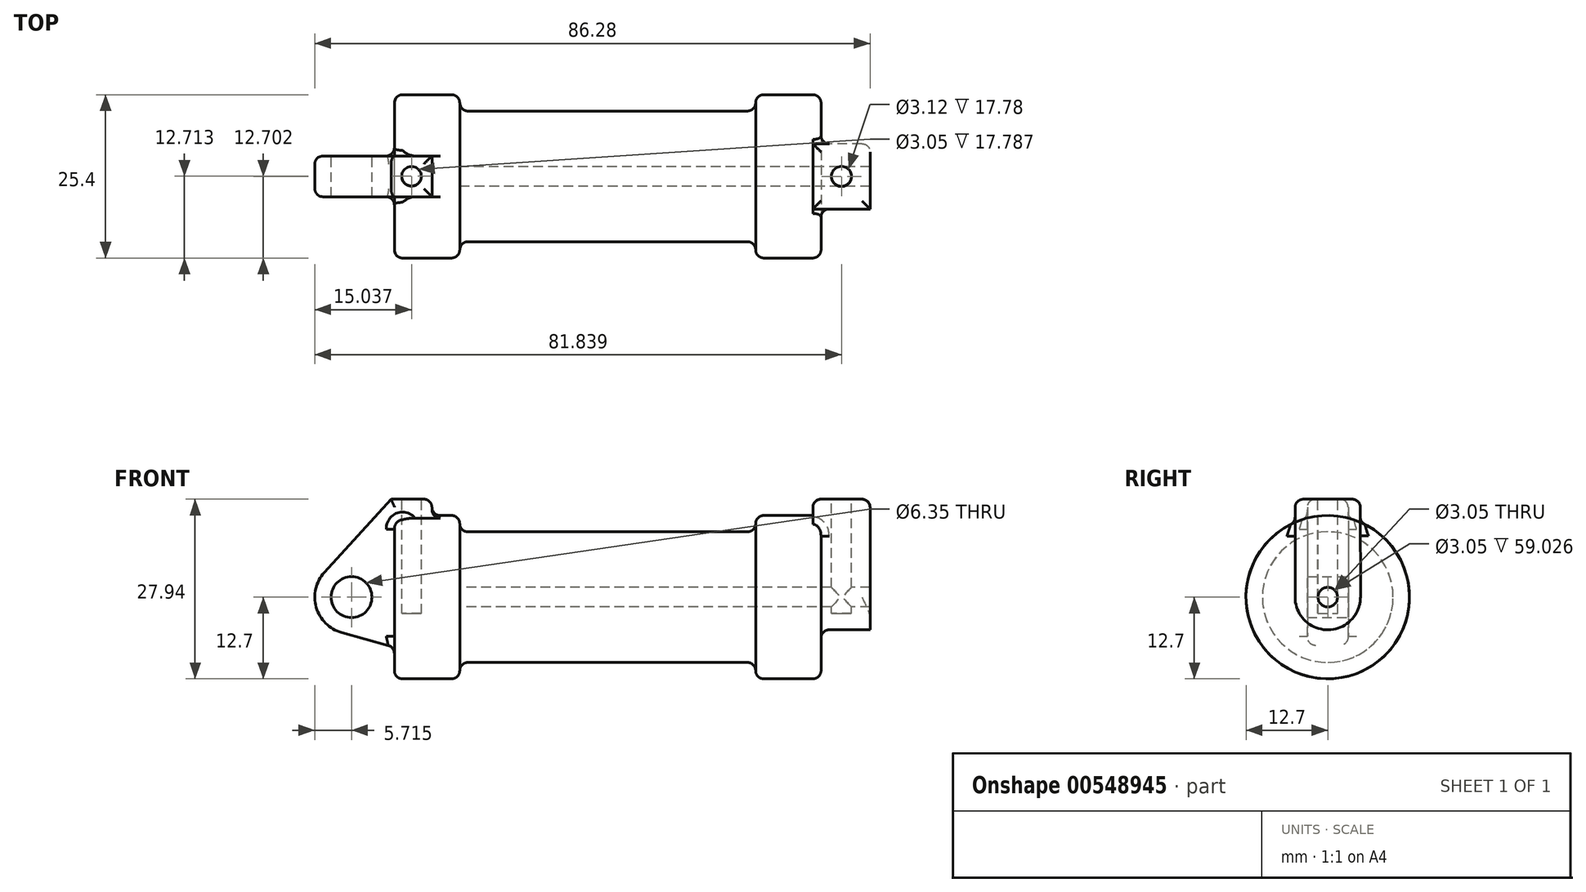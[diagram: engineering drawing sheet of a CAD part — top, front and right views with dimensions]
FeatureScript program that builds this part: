
annotation { "Feature Type Name" : "Feature", "Feature Type Description" : "" }
export const myFeature = defineFeature(function(context is Context, id is Id, definition is map)
    precondition{}
    {
        {
            var Q0;
            Q0=qCreatedBy(makeId("Front.planeOp"),FACE);
            var sketch = newSketch(context, id + "F0", { "sketchPlane" : qUnion([Q0])});
            skLineSegment(sketch, "E0", {"start": v(0, 0) * mm, "end": v(0, 12.7) * mm});
            skLineSegment(sketch, "E1", {"start": v(0, 12.7) * mm, "end": v(10.16, 12.7) * mm});
            skLineSegment(sketch, "E2", {"start": v(10.16, 12.7) * mm, "end": v(10.16, 10.16) * mm});
            skLineSegment(sketch, "E3", {"start": v(10.16, 10.16) * mm, "end": v(56.13, 10.16) * mm});
            skLineSegment(sketch, "E4", {"start": v(56.13, 10.16) * mm, "end": v(56.13, 12.7) * mm});
            skLineSegment(sketch, "E5", {"start": v(56.13, 12.7) * mm, "end": v(66.3, 12.7) * mm});
            skLineSegment(sketch, "E6", {"start": v(66.3, 12.7) * mm, "end": v(66.3, 0) * mm});
            skLineSegment(sketch, "E7", {"start": v(66.3, 0) * mm, "end": v(0, 0) * mm});
            skLineSegment(sketch, "E8", {"start": v(5.84, 15.24) * mm, "end": v(-0.5, 15.24) * mm});
            skLineSegment(sketch, "E9", {"start": v(-0.5, 15.24) * mm, "end": v(-10.88, 3.85) * mm});
            skLineSegment(sketch, "E10", {"start": v(0, 0) * mm, "end": v(-6.65, 0) * mm});
            skCircle(sketch, "E11", {"center": v(-6.65, 0) * mm, "radius": 5.72 * mm});
            skCircle(sketch, "E12", {"center": v(-6.65, 0) * mm, "radius": 3.18 * mm});
            skLineSegment(sketch, "E13", {"start": v(5.84, 15.24) * mm, "end": v(5.84, -9.4) * mm});
            skLineSegment(sketch, "E14", {"start": v(5.84, -9.4) * mm, "end": v(-8.18, -5.5) * mm});
            skSolve(sketch);
        }
        {
            var Q0;
            {var subQ0=sQuery(id+"F0.wireOp",EDGE,"E2");Q0=makeQuery(id+"F0.imprint","IMPRINT",FACE,{"disambiguationData":[TD([[makeQuery(id+"F0.imprint","IMPRINT",EDGE,{"derivedFrom":subQ0}),-1.0]])]});}
            var Q1;
            {var subQ0=sQuery(id+"F0.wireOp",EDGE,"E0");Q1=makeQuery(id+"F0.imprint","IMPRINT",FACE,{"disambiguationData":[TD([[makeQuery(id+"F0.imprint","IMPRINT",EDGE,{"derivedFrom":subQ0}),-1.0]])]});}
            var Q2;
            Q2=sQuery(id+"F0.wireOp",EDGE,"E10");
            revolve(context, id + "F1", {"entities" : qUnion([Q0, Q1]), "axis" : qUnion([Q2]), "revolveType" : RevolveType.FULL});
        }
        {
            var Q0;
            {var subQ1=sQuery(id+"F0.wireOp",EDGE,"E0");Q0=makeQuery(id+"F0.imprint","IMPRINT",FACE,{"disambiguationData":[TD([[makeQuery(id+"F0.imprint","IMPRINT",EDGE,{"derivedFrom":subQ1}),1.0]])]});}
            var Q1;
            {var subQ0=sQuery(id+"F0.wireOp",EDGE,"E0");Q1=makeQuery(id+"F0.imprint","IMPRINT",FACE,{"disambiguationData":[TD([[makeQuery(id+"F0.imprint","IMPRINT",EDGE,{"derivedFrom":subQ0}),-1.0]])]});}
            var Q2;
            {var subQ5=sQuery(id+"F0.wireOp",EDGE,"E12");Q2=makeQuery(id+"F0.imprint","IMPRINT",FACE,{"disambiguationData":[TD([[makeQuery(id+"F0.imprint","IMPRINT",EDGE,{"derivedFrom":subQ5}),-1.0]])]});}
            var Q3;
            {var subQ0=sQuery(id+"F0.wireOp",EDGE,"E14");Q3=makeQuery(id+"F0.imprint","IMPRINT",FACE,{"disambiguationData":[TD([[makeQuery(id+"F0.imprint","IMPRINT",EDGE,{"derivedFrom":subQ0}),-1.0]])]});}
            extrude(context, id + "F2", {"entities" : qUnion([Q0, Q1, Q2, Q3]), "operationType" : NewBodyOperationType.ADD, "endBound" : BoundingType.SYMMETRIC, "depth" : 6.35 * mm, "offsetDistance" : 25.4 * mm});
        }
        {
            var Q0;
            Q0=makeQuery(id+"F1.opRevolve","SWEPT_FACE",FACE,{"disambiguationData":[OSD([sQuery(id+"F0.wireOp",EDGE,"E6")])]});
            var sketch = newSketch(context, id + "F3", { "sketchPlane" : qUnion([Q0])});
            skCircle(sketch, "E15", {"center": v(0, 0) * mm, "radius": 1.52 * mm});
            skCircle(sketch, "E16", {"center": v(0, 0) * mm, "radius": 5.08 * mm});
            skLineSegment(sketch, "E17.left", {"start": v(-5.08, 0) * mm, "end": v(-5.08, 0) * mm});
            skLineSegment(sketch, "E17.right", {"start": v(5.08, 0) * mm, "end": v(5.08, 0) * mm});
            skLineSegment(sketch, "E18", {"start": v(5.08, 0) * mm, "end": v(5.06, 15.24) * mm});
            skLineSegment(sketch, "E19", {"start": v(5.06, 15.24) * mm, "end": v(-5.08, 15.23) * mm});
            skLineSegment(sketch, "E20", {"start": v(-5.08, 15.23) * mm, "end": v(-5.08, 0) * mm});
            skSolve(sketch);
        }
        {
            var Q0;
            {var subQ0=sQuery(id+"F3.wireOp",EDGE,"E19");Q0=makeQuery(id+"F3.imprint","IMPRINT",FACE,{"disambiguationData":[TD([[makeQuery(id+"F3.imprint","IMPRINT",EDGE,{"derivedFrom":subQ0}),1.0]])]});}
            var Q1;
            {var subQ0=sQuery(id+"F3.wireOp",EDGE,"E18");var subQ1=sQuery(id+"F3.wireOp",EDGE,"E16");var subQ2=makeQuery(id+"F3.imprint","INTERSECT",VERTEX,{"derivedFrom":[subQ1,subQ0]});Q1=makeQuery(id+"F3.imprint","IMPRINT",FACE,{"disambiguationData":[TD([[makeQuery(id+"F3.imprint","IMPRINT",EDGE,{"disambiguationData":[TD([[subQ2,-1.0]])],"derivedFrom":subQ1}),-1.0]])]});}
            var Q2;
            Q2=makeQuery(id+"F3.imprint","IMPRINT",FACE,{"disambiguationData":[TD([[makeQuery(id+"F3.imprint","IMPRINT",EDGE,{"derivedFrom":sQuery(id+"F3.wireOp",EDGE,"E15")}),-1.0]])]});
            extrude(context, id + "F4", {"entities" : qUnion([Q0, Q1, Q2]), "operationType" : NewBodyOperationType.ADD, "depth" : 7.62 * mm, "offsetDistance" : 25.4 * mm, "hasSecondDirection" : true, "secondDirectionOppositeDirection" : true, "secondDirectionDepth" : 1.27 * mm});
        }
        {
            var Q0;
            Q0=makeQuery(id+"F4.boolean.opBoolean","SPLIT",FACE,{"disambiguationData":[TD([makeQuery(id+"F4.opExtrude","SWEPT_FACE",FACE,{"disambiguationData":[OSD([sQuery(id+"F3.wireOp",EDGE,"E15")])]})])],"derivedFrom":makeQuery(id+"F1.opRevolve","SWEPT_FACE",FACE,{"disambiguationData":[OSD([sQuery(id+"F0.wireOp",EDGE,"E6")])]})});
            var Q1;
            Q1=makeQuery(id+"F1.opRevolve","SWEPT_FACE",FACE,{"disambiguationData":[OSD([sQuery(id+"F0.wireOp",EDGE,"E2")])]});
            extrude(context, id + "F5", {"entities" : qUnion([Q0]), "operationType" : NewBodyOperationType.REMOVE, "endBound" : BoundingType.UP_TO_SURFACE, "oppositeDirection" : true, "depth" : 25.4 * mm, "endBoundEntityFace" : qUnion([Q1]), "offsetDistance" : 25.4 * mm});
        }
        {
            var Q0;
            Q0=makeQuery(id+"F4.opExtrude","SWEPT_FACE",FACE,{"disambiguationData":[OSD([sQuery(id+"F3.wireOp",EDGE,"E19")])]});
            var sketch = newSketch(context, id + "F6", { "sketchPlane" : qUnion([Q0])});
            skCircle(sketch, "E21", {"center": v(2.67, 0.02) * mm, "radius": 1.52 * mm});
            skCircle(sketch, "E22", {"center": v(69.47, 0.01) * mm, "radius": 1.56 * mm});
            skSolve(sketch);
        }
        {
            var Q0;
            Q0=makeQuery(id+"F6.imprint","IMPRINT",FACE,{"disambiguationData":[TD([[makeQuery(id+"F6.imprint","IMPRINT",EDGE,{"derivedFrom":sQuery(id+"F6.wireOp",EDGE,"E22")}),1.0]])]});
            extrude(context, id + "F7", {"entities" : qUnion([Q0]), "operationType" : NewBodyOperationType.REMOVE, "oppositeDirection" : true, "depth" : 10.4 * mm, "offsetDistance" : 25.4 * mm});
        }
        {
            var Q0;
            Q0 = qSketchRegion(id + "F6", true);
            extrude(context, id + "F8", {"entities" : qUnion([Q0]), "operationType" : NewBodyOperationType.REMOVE, "oppositeDirection" : true, "depth" : 17.78 * mm, "offsetDistance" : 25.4 * mm});
        }
        {
            var Q0;
            Q0=makeQuery(id+"F4.opExtrude","CAP_EDGE",EDGE,{"disambiguationData":[OSD([sQuery(id+"F3.wireOp",EDGE,"E19")])],"isStart":true});
            var Q1;
            Q1=makeQuery(id+"F4.opExtrude","SWEPT_EDGE",EDGE,{"disambiguationData":[OSD([sQuery(id+"F3.wireOp",EDGE,"E18"),sQuery(id+"F3.wireOp",EDGE,"E19")])]});
            var Q2;
            Q2=makeQuery(id+"F4.opExtrude","CAP_EDGE",EDGE,{"disambiguationData":[OSD([sQuery(id+"F3.wireOp",EDGE,"E19")])],"isStart":false});
            var Q3;
            Q3=makeQuery(id+"F4.opExtrude","SWEPT_EDGE",EDGE,{"disambiguationData":[OSD([sQuery(id+"F3.wireOp",EDGE,"E19"),sQuery(id+"F3.wireOp",EDGE,"E20")])]});
            var Q4;
            Q4=makeQuery(id+"F4.opExtrude","CAP_EDGE",EDGE,{"disambiguationData":[OSD([sQuery(id+"F3.wireOp",EDGE,"E18")])],"isStart":false});
            var Q5;
            Q5=makeQuery(id+"F4.boolean.opBoolean","SPLIT",FACE,{"disambiguationData":[TD([makeQuery(id+"F1.opRevolve","SWEPT_FACE",FACE,{"disambiguationData":[OSD([sQuery(id+"F0.wireOp",EDGE,"E5")])]})])],"derivedFrom":makeQuery(id+"F1.opRevolve","SWEPT_FACE",FACE,{"disambiguationData":[OSD([sQuery(id+"F0.wireOp",EDGE,"E6")])]})});
            var Q6;
            Q6=makeQuery(id+"F1.opRevolve","SWEPT_FACE",FACE,{"disambiguationData":[OSD([sQuery(id+"F0.wireOp",EDGE,"E4")])]});
            var Q7;
            Q7=makeQuery(id+"F1.opRevolve","SWEPT_FACE",FACE,{"disambiguationData":[OSD([sQuery(id+"F0.wireOp",EDGE,"E2")])]});
            var Q8;
            Q8=makeQuery(id+"F1.opRevolve","SWEPT_FACE",FACE,{"disambiguationData":[OSD([sQuery(id+"F0.wireOp",EDGE,"E0")])]});
            var Q9;
            Q9=makeQuery(id+"F2.opExtrude","CAP_EDGE",EDGE,{"disambiguationData":[OSD([sQuery(id+"F0.wireOp",EDGE,"E9")])],"isStart":false});
            var Q10;
            Q10=makeQuery(id+"F2.opExtrude","CAP_EDGE",EDGE,{"disambiguationData":[OSD([sQuery(id+"F0.wireOp",EDGE,"E9")])],"isStart":true});
            var Q11;
            Q11=makeQuery(id+"F2.opExtrude","SWEPT_EDGE",EDGE,{"disambiguationData":[OSD([sQuery(id+"F0.wireOp",EDGE,"E8"),sQuery(id+"F0.wireOp",EDGE,"E13")])]});
            var Q12;
            Q12=makeQuery(id+"F2.opExtrude","CAP_EDGE",EDGE,{"disambiguationData":[OSD([sQuery(id+"F0.wireOp",EDGE,"E8")])],"isStart":false});
            var Q13;
            Q13=makeQuery(id+"F2.opExtrude","CAP_EDGE",EDGE,{"disambiguationData":[OSD([sQuery(id+"F0.wireOp",EDGE,"E8")])],"isStart":true});
            var Q14;
            Q14=makeQuery(id+"F2.boolean.opBoolean","INTERSECT",EDGE,{"derivedFrom":[makeQuery(id+"F1.opRevolve","SWEPT_FACE",FACE,{"disambiguationData":[OSD([sQuery(id+"F0.wireOp",EDGE,"E1")])]}),makeQuery(id+"F2.opExtrude","SWEPT_FACE",FACE,{"disambiguationData":[OSD([sQuery(id+"F0.wireOp",EDGE,"E13")])]})]});
            fillet(context, id + "F9", {"entities" : qUnion([Q0, Q1, Q2, Q3, Q4, Q5, Q6, Q7, Q8, Q9, Q10, Q11, Q12, Q13, Q14]), "radius" : 1.27 * mm, "tangentPropagation" : true, "allowEdgeOverflow" : false});
        }
    });
